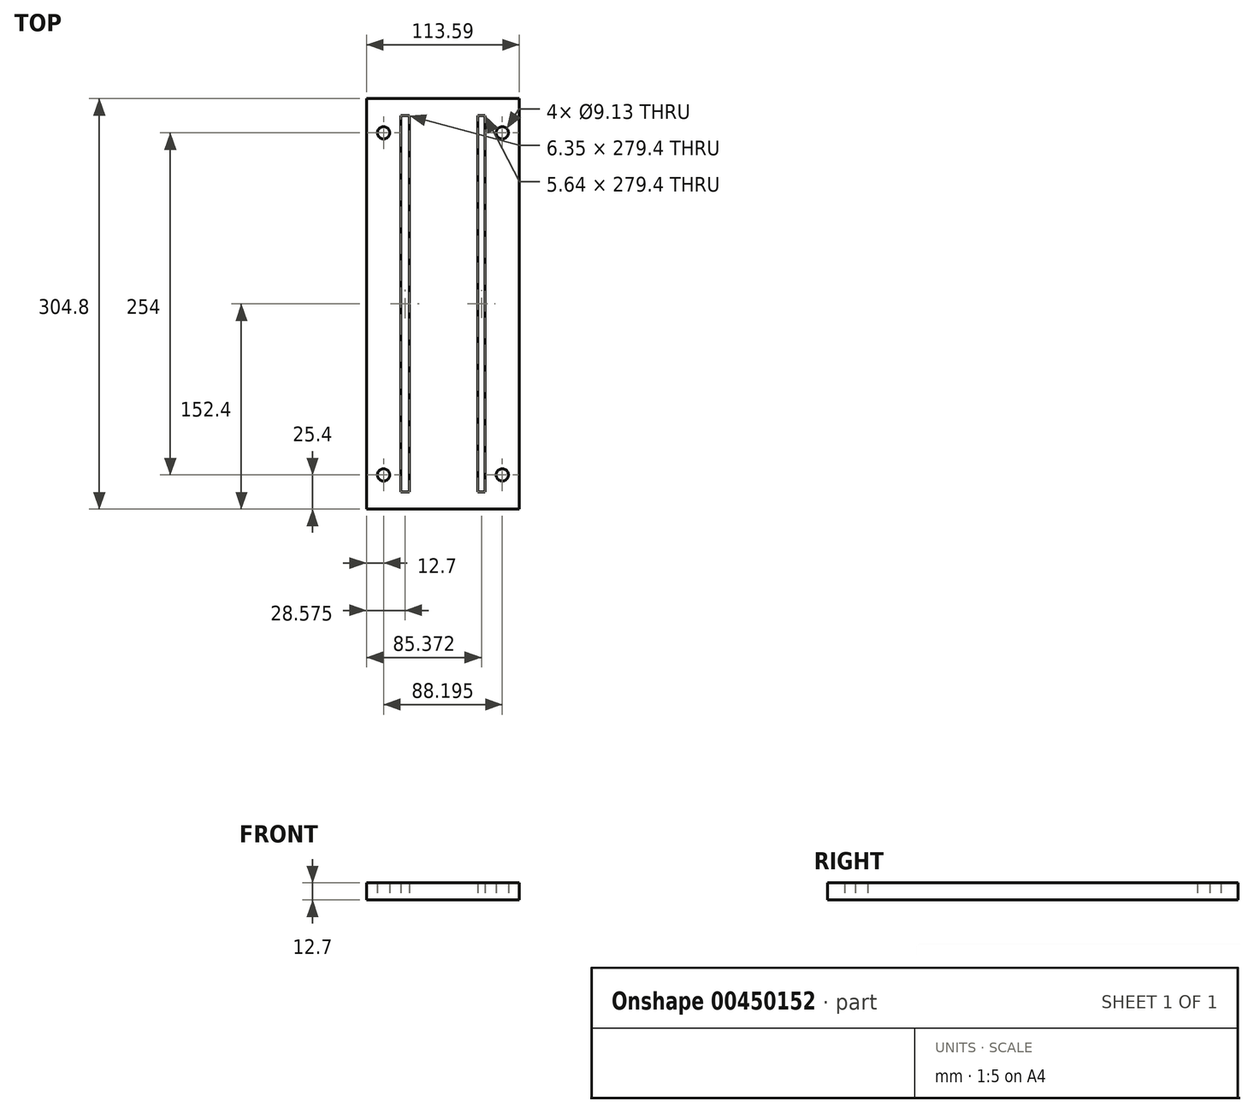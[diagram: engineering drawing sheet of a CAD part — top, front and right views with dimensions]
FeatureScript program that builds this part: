
annotation { "Feature Type Name" : "Feature", "Feature Type Description" : "" }
export const myFeature = defineFeature(function(context is Context, id is Id, definition is map)
    precondition{}
    {
        {
            var Q0;
            Q0=qCreatedBy(makeId("Top.planeOp"),FACE);
            var sketch = newSketch(context, id + "F0", { "sketchPlane" : qUnion([Q0])});
            skLineSegment(sketch, "E0.bottom", {"start": v(56.44, 152.4) * mm, "end": v(-57.15, 152.4) * mm});
            skLineSegment(sketch, "E0.top", {"start": v(56.44, -152.4) * mm, "end": v(-57.15, -152.4) * mm});
            skLineSegment(sketch, "E0.left", {"start": v(56.44, 152.4) * mm, "end": v(56.44, -152.4) * mm});
            skLineSegment(sketch, "E0.right", {"start": v(-57.15, 152.4) * mm, "end": v(-57.15, -152.4) * mm});
            skPoint(sketch, "E0.middle", {"position": v(0, 0) * mm});
            skCircle(sketch, "E1", {"center": v(43.74, -127) * mm, "radius": 4.56 * mm});
            skCircle(sketch, "E2", {"center": v(-44.45, -127) * mm, "radius": 4.56 * mm});
            skCircle(sketch, "E3", {"center": v(43.74, 127) * mm, "radius": 4.56 * mm});
            skCircle(sketch, "E4", {"center": v(-44.45, 127) * mm, "radius": 4.56 * mm});
            skLineSegment(sketch, "E5.bottom", {"start": v(-31.75, 139.7) * mm, "end": v(-25.4, 139.7) * mm});
            skLineSegment(sketch, "E5.top", {"start": v(-31.75, -139.7) * mm, "end": v(-25.4, -139.7) * mm});
            skLineSegment(sketch, "E5.left", {"start": v(-31.75, 139.7) * mm, "end": v(-31.75, -139.7) * mm});
            skLineSegment(sketch, "E5.right", {"start": v(-25.4, 139.7) * mm, "end": v(-25.4, -139.7) * mm});
            skLineSegment(sketch, "E6.bottom", {"start": v(25.4, 139.7) * mm, "end": v(31.04, 139.7) * mm});
            skLineSegment(sketch, "E6.top", {"start": v(25.4, -139.7) * mm, "end": v(31.04, -139.7) * mm});
            skLineSegment(sketch, "E6.left", {"start": v(25.4, 139.7) * mm, "end": v(25.4, -139.7) * mm});
            skLineSegment(sketch, "E6.right", {"start": v(31.04, 139.7) * mm, "end": v(31.04, -139.7) * mm});
            skSolve(sketch);
        }
        {
            var Q0;
            Q0=makeQuery(id+"F0.imprint","IMPRINT",FACE,{"disambiguationData":[TD([[makeQuery(id+"F0.imprint","IMPRINT",EDGE,{"derivedFrom":sQuery(id+"F0.wireOp",EDGE,"E0.bottom")}),1.0]])]});
            extrude(context, id + "F1", {"entities" : qUnion([Q0]), "depth" : 12.7 * mm});
        }
    });
